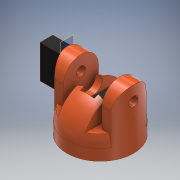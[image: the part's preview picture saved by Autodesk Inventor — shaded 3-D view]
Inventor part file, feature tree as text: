
AUTODESK INVENTOR PART (.ipt)
format: ipt  version: 2017 (Build 210142000, 142)  size: 254,464 bytes
history: native  units: mm
features: sketch x14, extrude x13, plane x9, revolve x1, mirror x1
ambient origin geometry x8: Origin, YZ Plane, XZ Plane, XY Plane, X Axis, Y Axis, Z Axis, Center Point
bodies: Solid1 (feature_tree)
feature tree (38):
  extrude  "Extrusion1"  Depth=18.0mm TaperAngle=0.0deg
  plane  "Work Plane1"
  revolve  "Revolution1"  Angle=90.0deg
  plane  "Work Plane3"
  extrude  "Extrusion5"  Depth=60.0mm TaperAngle=0.0deg
  sketch  "Sketch12"  dims[d35=18.0mm d36=0.0mm d37=18.0mm d38=0.0mm]
  extrude  "Extrusion6"  Depth=18.0mm TaperAngle=0.0deg
  extrude  "Extrusion7"  Depth=22.5mm TaperAngle=0.0deg
  extrude  "Extrusion8"  Depth=22.5mm TaperAngle=0.0deg
  plane  "Work Plane4"
  extrude  "Extrusion9"  [1 undecoded]
  extrude  "Extrusion10"  Depth=15.0mm
  sketch  "Sketch20"  dims[d57=22.5mm d58=0.0mm d60=15.0mm]
  plane  "Work Plane6"
  extrude  "Extrusion11"  Depth=60.0mm TaperAngle=0.0deg
  plane  "Work Plane7"
  extrude  "Extrusion12"  Depth=33.0mm TaperAngle=0.0deg
  plane  "Work Plane8"
  mirror  "Mirror1"
  plane  "Work Plane9"
  extrude  "Extrusion13"  [1 undecoded]
  extrude  "Extrusion14"  [1 undecoded]
  extrude  "Extrusion15"  [1 undecoded]
  plane  "Work Plane13"
  extrude  "Extrusion16"  [1 undecoded]
  sketch  "Sketch1"  dims[d0=107.0mm d1=18.0mm d2=0.0mm]
  sketch  "Sketch2"  dims[d3=0.0mm d4=90.0deg]
  plane  "Work Plane2"
  sketch  "Sketch11"  dims[d5=0.0mm d6=36.0mm d27=60.0mm d28=0.0mm]
  sketch  "Sketch13"  dims[d39=77.5mm d40=0.0mm d43=22.5mm d44=0.0mm]
  sketch  "Sketch18"  dims[d46=22.5mm d47=0.0mm d49=22.5mm d50=0.0mm]
  sketch  "Sketch19"  dims[d54=44.0mm d55=0.0mm d56=-22.0mm]
  sketch  "Sketch21"  dims[d61=72.2mm d65=60.0mm d66=0.0mm]
  sketch  "Sketch23"  dims[d70=13.0mm d71=0.0mm d75=33.0mm d76=0.0mm]
  sketch  "Sketch24"
  sketch  "Sketch27"
  sketch  "Sketch28"
  sketch  "Sketch29"
note: 5 required parameter values undecoded (feature->parameter linkage not recoverable at this tier; creation-order binding heuristic only, values carry confidence <= 0.55)
